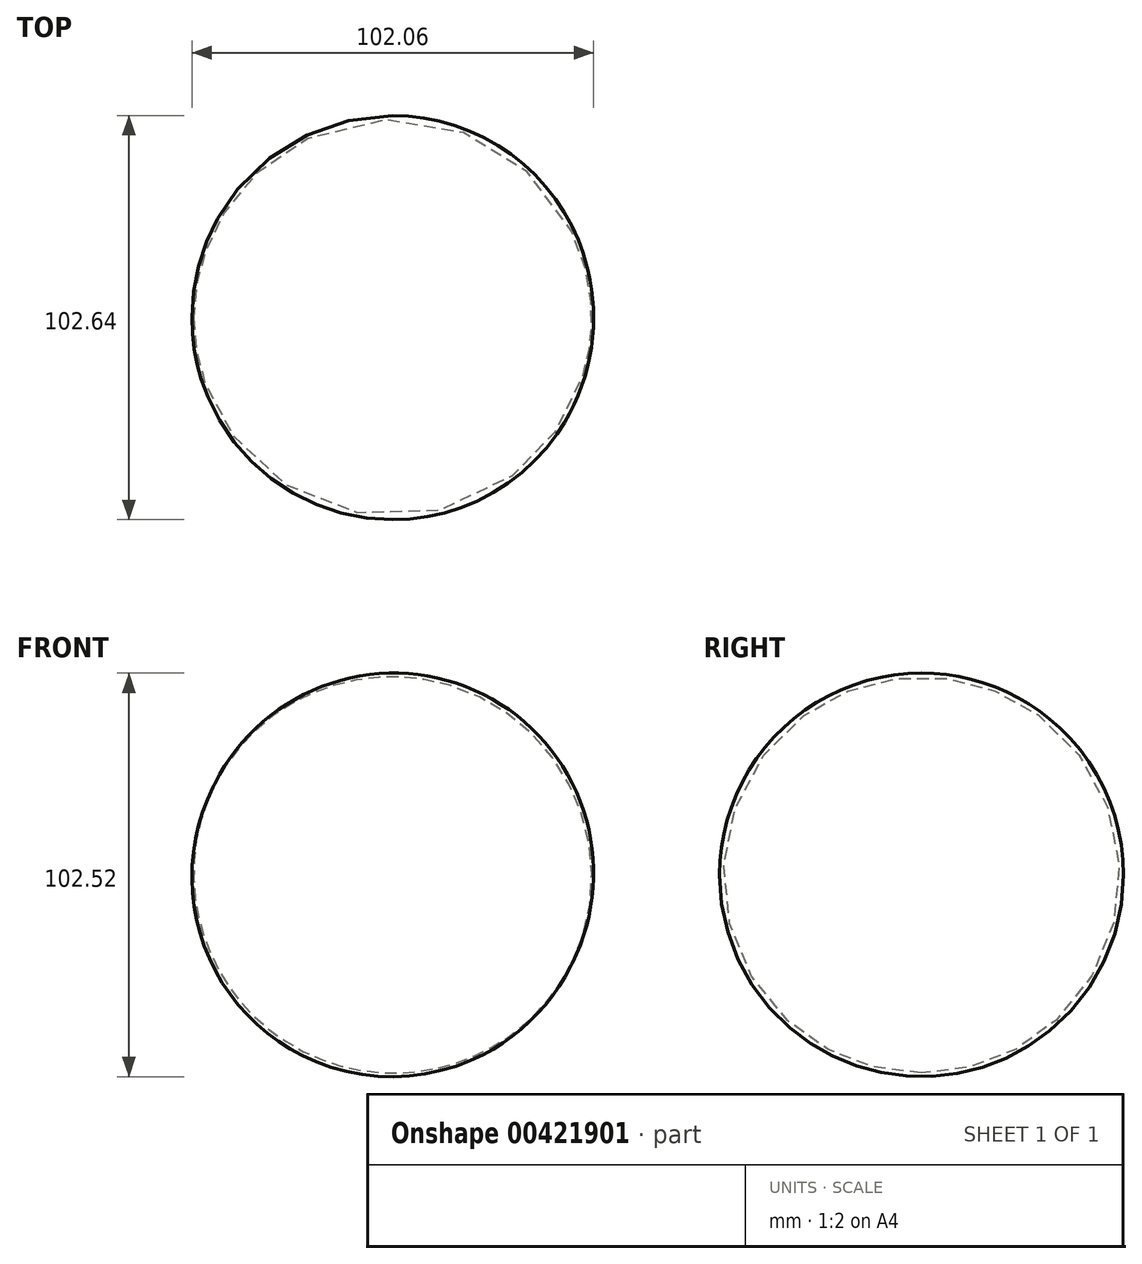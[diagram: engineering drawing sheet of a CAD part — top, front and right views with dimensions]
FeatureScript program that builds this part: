
annotation { "Feature Type Name" : "Feature", "Feature Type Description" : "" }
export const myFeature = defineFeature(function(context is Context, id is Id, definition is map)
    precondition{}
    {
        {
            var Q0;
            Q0=qCreatedBy(makeId("Front.planeOp"),FACE);
            var sketch = newSketch(context, id + "F0", { "sketchPlane" : qUnion([Q0])});
            skArc(sketch, "E0", {"start": v(-39.87, 1.8) * mm, "mid": v(-17.55, -66.88) * mm, "end": v(50.89, -43.87) * mm});
            skLineSegment(sketch, "E1", {"start": v(-39.87, 1.8) * mm, "end": v(50.89, -43.87) * mm});
            skPoint(sketch, "E2.orphan", {"position": v(0, 29.03) * mm});
            skSolve(sketch);
        }
        {
            var Q0;
            Q0=makeQuery(id+"F0.imprint","IMPRINT",FACE,{"disambiguationData":[TD([[makeQuery(id+"F0.imprint","IMPRINT",EDGE,{"derivedFrom":sQuery(id+"F0.wireOp",EDGE,"E0")}),1.0]])]});
            var Q1;
            Q1=sQuery(id+"F0.wireOp",EDGE,"E1");
            revolve(context, id + "F1", {"entities" : qUnion([Q0]), "axis" : qUnion([Q1]), "revolveType" : RevolveType.FULL});
        }
    });
